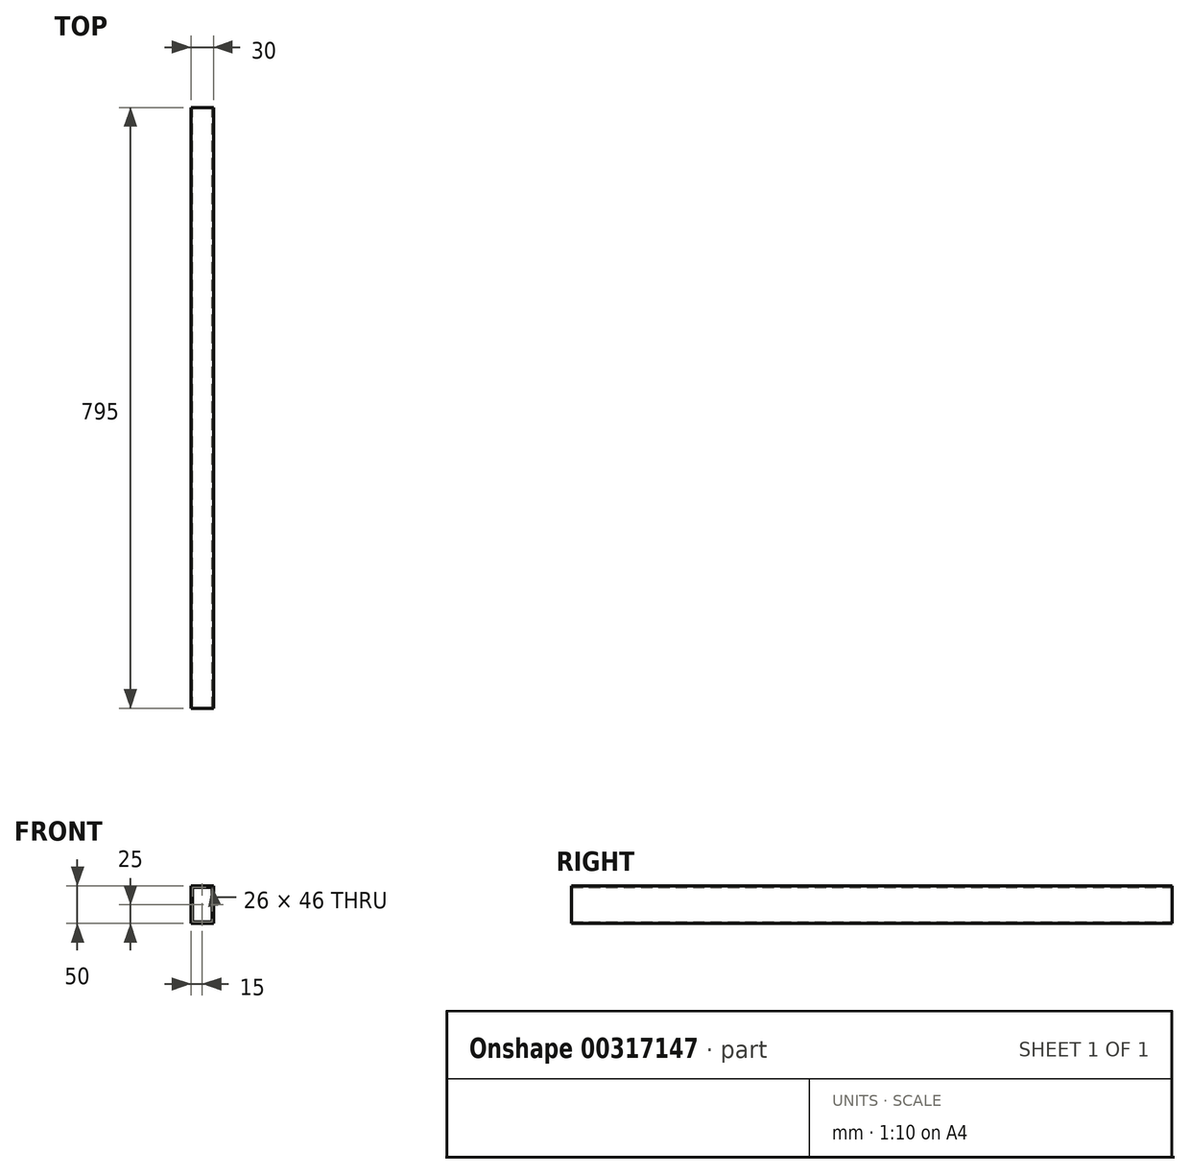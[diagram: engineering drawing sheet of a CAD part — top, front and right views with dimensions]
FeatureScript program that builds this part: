
annotation { "Feature Type Name" : "Feature", "Feature Type Description" : "" }
export const myFeature = defineFeature(function(context is Context, id is Id, definition is map)
    precondition{}
    {
        {
            var Q0;
            Q0=qCreatedBy(makeId("Front.planeOp"),FACE);
            var sketch = newSketch(context, id + "F0", { "sketchPlane" : qUnion([Q0])});
            skLineSegment(sketch, "E0.bottom", {"start": v(15, 25) * mm, "end": v(-15, 25) * mm});
            skLineSegment(sketch, "E0.top", {"start": v(15, -25) * mm, "end": v(-15, -25) * mm});
            skLineSegment(sketch, "E0.left", {"start": v(15, 25) * mm, "end": v(15, -25) * mm});
            skLineSegment(sketch, "E0.right", {"start": v(-15, 25) * mm, "end": v(-15, -25) * mm});
            skPoint(sketch, "E0.middle", {"position": v(0, 0) * mm});
            skLineSegment(sketch, "E1.0", {"start": v(13, -23) * mm, "end": v(-13, -23) * mm});
            skLineSegment(sketch, "E1.1", {"start": v(13, 23) * mm, "end": v(13, -23) * mm});
            skLineSegment(sketch, "E1.2", {"start": v(13, 23) * mm, "end": v(-13, 23) * mm});
            skLineSegment(sketch, "E1.3", {"start": v(-13, 23) * mm, "end": v(-13, -23) * mm});
            skSolve(sketch);
        }
        {
            var Q0;
            Q0=makeQuery(id+"F0.imprint","IMPRINT",FACE,{"disambiguationData":[TD([[makeQuery(id+"F0.imprint","IMPRINT",EDGE,{"derivedFrom":sQuery(id+"F0.wireOp",EDGE,"E0.bottom")}),1.0]])]});
            extrude(context, id + "F1", {"entities" : qUnion([Q0]), "endBound" : BoundingType.SYMMETRIC, "depth" : (845 - 50) * mm});
        }
    });
